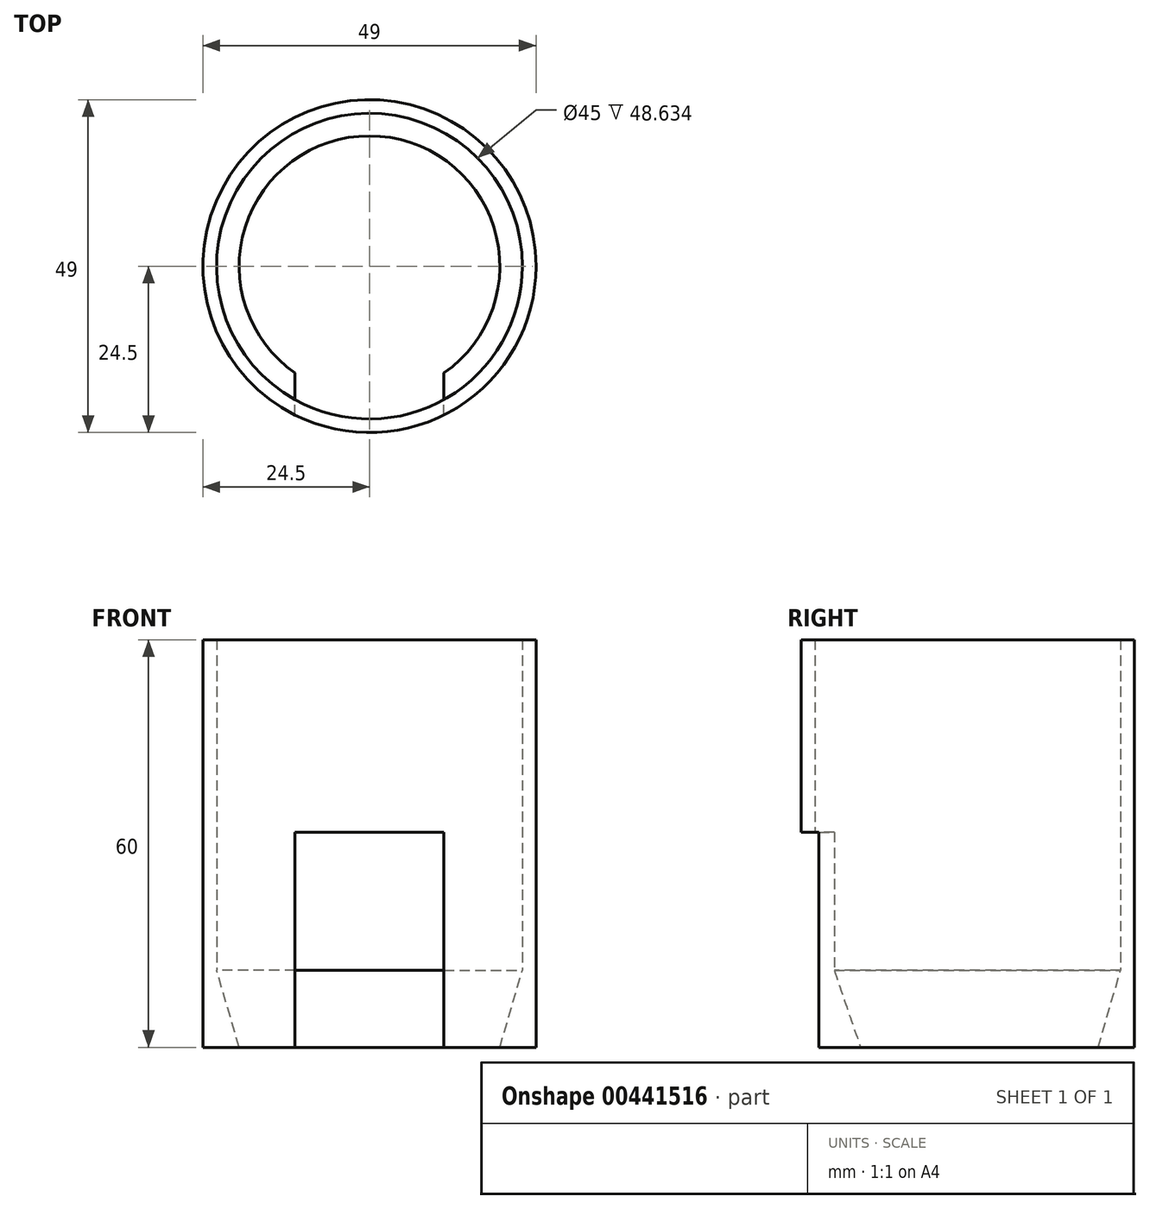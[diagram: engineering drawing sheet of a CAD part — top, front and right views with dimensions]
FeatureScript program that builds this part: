
annotation { "Feature Type Name" : "Feature", "Feature Type Description" : "" }
export const myFeature = defineFeature(function(context is Context, id is Id, definition is map)
    precondition{}
    {
        {
            var Q0;
            Q0=qCreatedBy(makeId("Top.planeOp"),FACE);
            var sketch = newSketch(context, id + "F0", { "sketchPlane" : qUnion([Q0])});
            skCircle(sketch, "E0", {"center": v(0, 0) * mm, "radius": 24.5 * mm});
            skCircle(sketch, "E1.0", {"center": v(0, 0) * mm, "radius": 22.5 * mm});
            skSolve(sketch);
        }
        {
            var Q0;
            Q0 = qSketchRegion(id + "F0", true);
            extrude(context, id + "F1", {"entities" : qUnion([Q0]), "depth" : 60 * mm});
        }
        {
            var Q0;
            Q0=qCreatedBy(makeId("Front.planeOp"),FACE);
            var sketch = newSketch(context, id + "F2", { "sketchPlane" : qUnion([Q0])});
            skLineSegment(sketch, "E2", {"start": v(22.54, 11.5) * mm, "end": v(19.18, 0) * mm});
            skLineSegment(sketch, "E3", {"start": v(22.54, 11.5) * mm, "end": v(23.44, 11.5) * mm});
            skLineSegment(sketch, "E4", {"start": v(23.44, 11.5) * mm, "end": v(23.44, 0) * mm});
            skLineSegment(sketch, "E5", {"start": v(23.44, 0) * mm, "end": v(19.18, 0) * mm});
            skLineSegment(sketch, "E6", {"start": v(0, 14.65) * mm, "end": v(0, 2.68) * mm, "construction": true});
            skSolve(sketch);
        }
        {
            var Q0;
            Q0 = qSketchRegion(id + "F2", true);
            var Q1;
            Q1=sQuery(id+"F2.wireOp",EDGE,"E6");
            revolve(context, id + "F3", {"operationType" : NewBodyOperationType.ADD, "entities" : qUnion([Q0]), "axis" : qUnion([Q1]), "revolveType" : RevolveType.FULL});
        }
        {
            var Q0;
            Q0=qCreatedBy(makeId("Front.planeOp"),FACE);
            var sketch = newSketch(context, id + "F4", { "sketchPlane" : qUnion([Q0])});
            skLineSegment(sketch, "E7.bottom", {"start": v(-10.96, -4.23) * mm, "end": v(10.96, -4.23) * mm});
            skLineSegment(sketch, "E7.top", {"start": v(-10.96, 31.68) * mm, "end": v(10.96, 31.68) * mm});
            skLineSegment(sketch, "E7.left", {"start": v(-10.96, -4.23) * mm, "end": v(-10.96, 31.68) * mm});
            skLineSegment(sketch, "E7.right", {"start": v(10.96, -4.23) * mm, "end": v(10.96, 31.68) * mm});
            skSolve(sketch);
        }
        {
            var Q0;
            Q0 = qSketchRegion(id + "F4", true);
            extrude(context, id + "F5", {"entities" : qUnion([Q0]), "operationType" : NewBodyOperationType.REMOVE, "depth" : 25 * mm});
        }
    });
